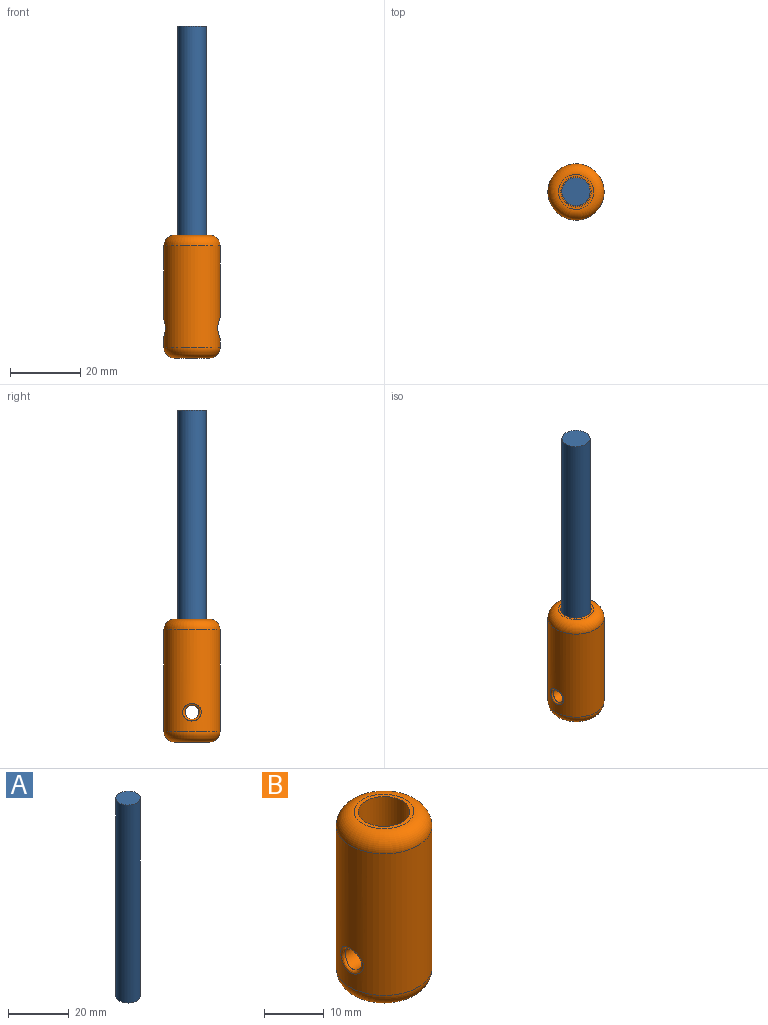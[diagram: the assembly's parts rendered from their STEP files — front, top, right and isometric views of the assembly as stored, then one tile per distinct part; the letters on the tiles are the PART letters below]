
ASSEMBLY  parts=2 mates=1
PART A: 3 faces, bbox 8x8x79.7 mm
  f0: cylinder r=4mm len=79.65mm, axis (0,0,-1), area 2001.8mm2, adj f1,f2
  f1: plane 8x8mm, normal (0,0,1), area 50.3mm2, adj f0
  f2: plane 8x8mm, normal (0,0,-1), area 50.3mm2, adj f0
PART B: 10 faces, bbox 17.3x17.3x35 mm
  f0: cylinder r=8mm len=29mm, axis (0,0,-1), area 1403.3mm2, adj f5,f6,f8,f9
  f1: plane 10x10mm, normal (0,0,1), area 19.8mm2, adj f3,f5
  f2: plane 10x10mm, normal (0,0,-1), area 78.5mm2, adj f6
  f3: cylinder r=4.33mm len=20mm, axis (0,0,1), area 543.5mm2, adj f1,f4
  f4: plane 8.65x8.65mm, normal (0,0,1), area 58.8mm2, adj f3
  f5: torus R=5mm, axis (0,0,1), area 204.6mm2, adj f0,f1
  f6: torus R=5mm, axis (0,0,1), area 204.6mm2, adj f0,f2
  f7: cylinder r=2mm len=14.5mm, axis (1,0,0), area 175.3mm2, adj f8,f9
  f8: bspline ~6.87x6mm, area 27.9mm2, adj f0,f7
  f9: bspline ~5.34x5.01mm, area 12.2mm2, adj f0,f7
PLACE A t=(0,0,15)mm
PLACE B at identity fixed
MATE fastened B.f3 <-> A.f0  axis (0,0,1) through (0,0,15)mm
